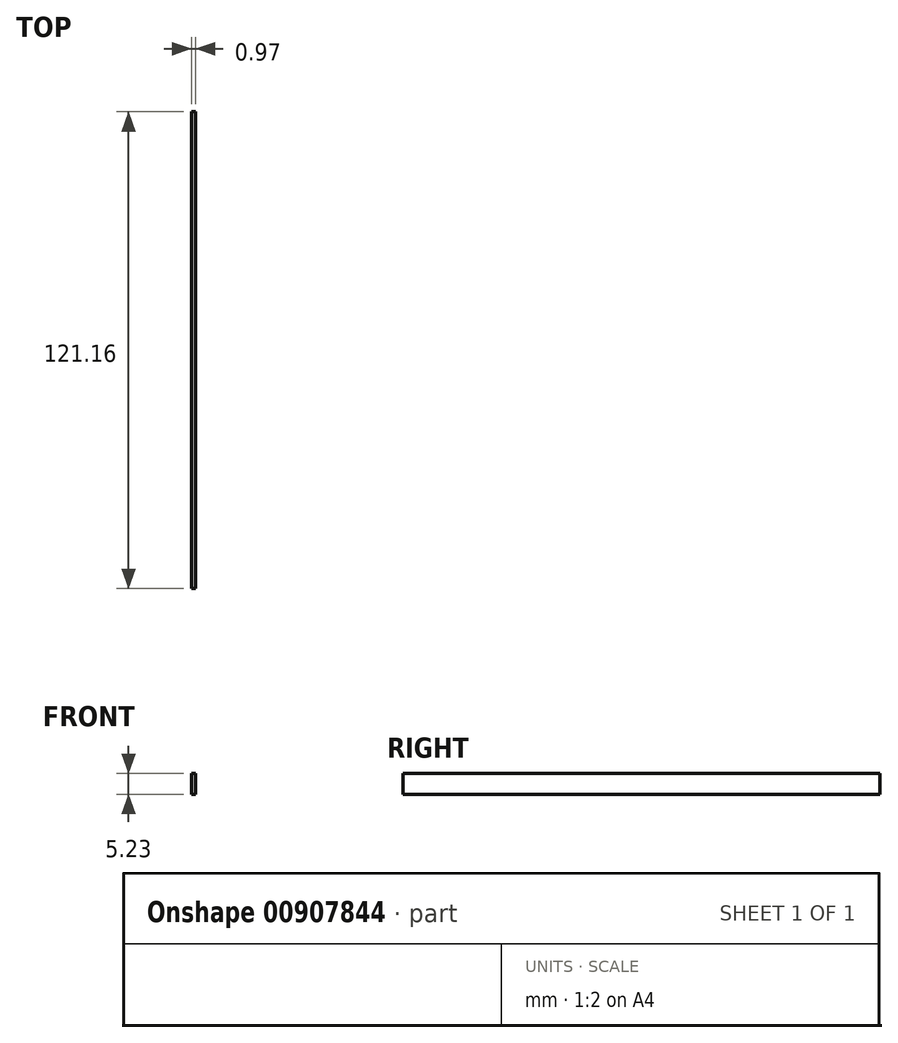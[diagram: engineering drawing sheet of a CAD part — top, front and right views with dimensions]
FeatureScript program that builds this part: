
annotation { "Feature Type Name" : "Feature", "Feature Type Description" : "" }
export const myFeature = defineFeature(function(context is Context, id is Id, definition is map)
    precondition{}
    {
        {
            var Q0;
            Q0=qCreatedBy(makeId("Front.planeOp"),FACE);
            var sketch = newSketch(context, id + "F0", { "sketchPlane" : qUnion([Q0])});
            skLineSegment(sketch, "E0.bottom", {"start": v(-98.75, 13.1) * mm, "end": v(-97.78, 13.1) * mm});
            skLineSegment(sketch, "E0.top", {"start": v(-98.75, 7.87) * mm, "end": v(-97.78, 7.87) * mm});
            skLineSegment(sketch, "E0.left", {"start": v(-98.75, 13.1) * mm, "end": v(-98.75, 7.87) * mm});
            skLineSegment(sketch, "E0.right", {"start": v(-97.78, 13.1) * mm, "end": v(-97.78, 7.87) * mm});
            skSolve(sketch);
        }
        {
            var Q0;
            Q0 = qSketchRegion(id + "F0", true);
            extrude(context, id + "F1", {"entities" : qUnion([Q0]), "depth" : 121.16 * mm, "offsetDistance" : 25.4 * mm});
        }
    });
